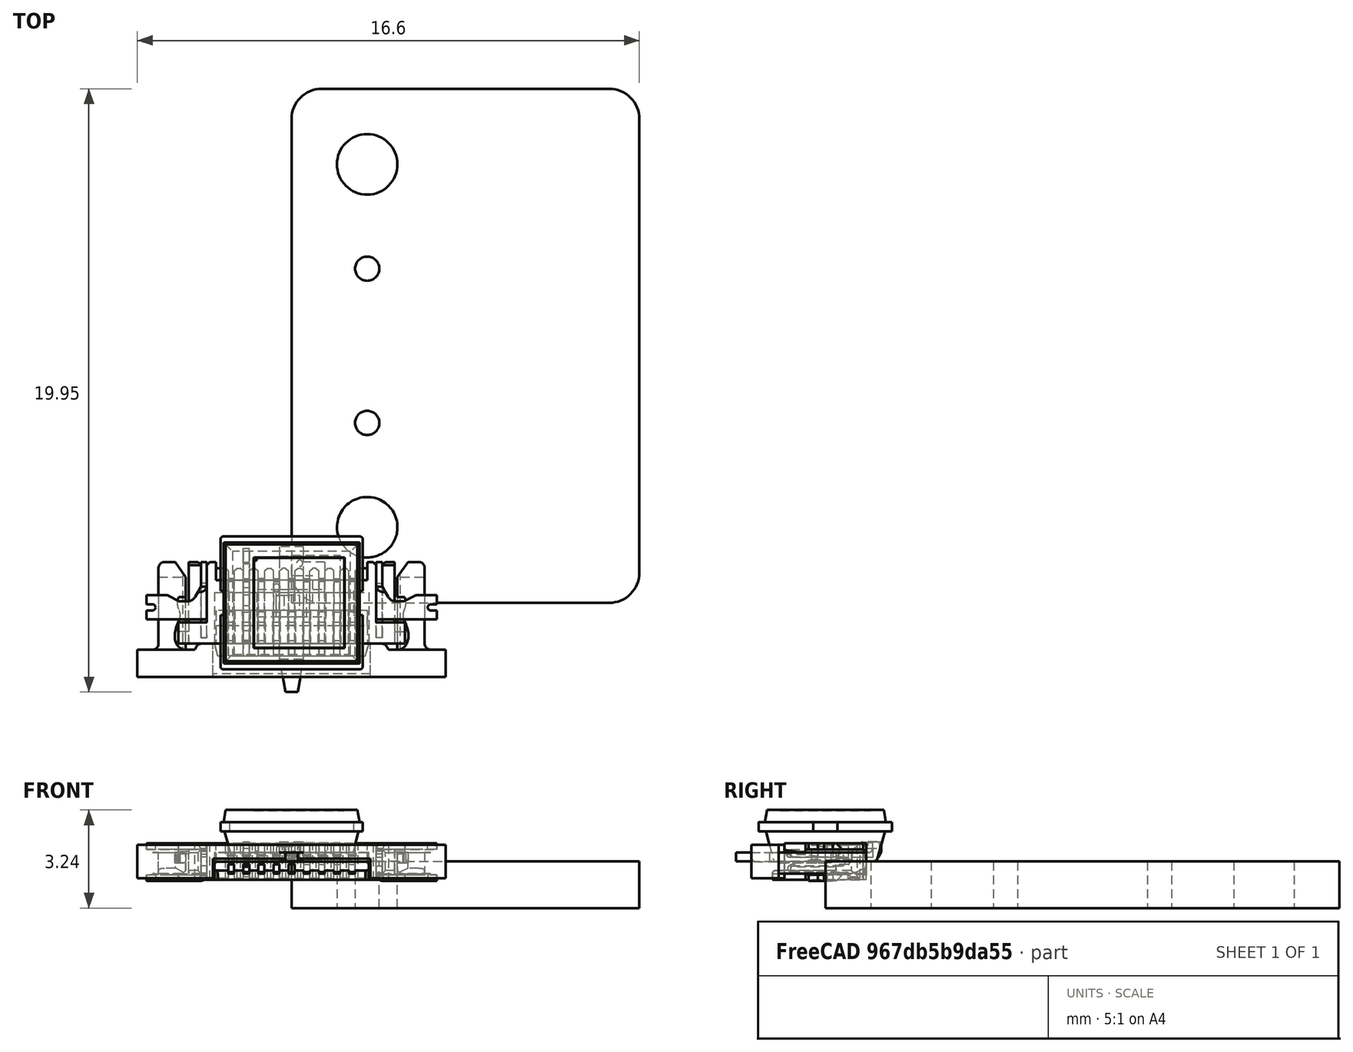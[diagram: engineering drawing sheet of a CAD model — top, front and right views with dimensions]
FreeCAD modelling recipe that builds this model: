
FCSTD DOCUMENT  (FreeCAD 0.20R29603 (Git))
Label: sensor-PCB
License: All rights reserved
LicenseURL: http://en.wikipedia.org/wiki/All_rights_reserved
objects: Part::Feature×21, App::Part×16, App::Link×15, Part::Compound2×3, PartDesign::SubShapeBinder×2, PartDesign::CoordinateSystem×2, App::FeaturePython×1, PartDesign::Body×1
note: 26 computed .brp shape members not serialized (recipe doc carries the construction recipe); baked Part::Feature solids carry a one-line shape summary decoded from their .brp

FEATURE [App::FeaturePython] Constraints  # WARN: FeaturePython — macro-defined, semantics opaque (R4)
  _Version = 1
FEATURE [App::Link] Link  label="ball001"
  LinkPlacement = pos=(0,0.5,0.125) rot=(0,0,1;0rad)
  LinkedObject = -> Solid002
  Placement = pos=(0,0.5,0.125) rot=(0,0,1;0rad)
FEATURE [App::Link] Link001  label="ball002"
  LinkPlacement = pos=(0.5,0.5,0.125) rot=(0,0,1;0rad)
  LinkedObject = -> Solid002
  Placement = pos=(0.5,0.5,0.125) rot=(0,0,1;0rad)
FEATURE [App::Link] Link002  label="ball003"
  LinkPlacement = pos=(-0.5,0,0.125) rot=(0,0,1;0rad)
  LinkedObject = -> Solid002
  Placement = pos=(-0.5,0,0.125) rot=(0,0,1;0rad)
FEATURE [App::Link] Link003  label="ball004"
  LinkPlacement = pos=(0,0,0.125) rot=(0,0,1;0rad)
  LinkedObject = -> Solid002
  Placement = pos=(0,0,0.125) rot=(0,0,1;0rad)
FEATURE [App::Link] Link004  label="ball005"
  LinkPlacement = pos=(0.5,0,0.125) rot=(0,0,1;0rad)
  LinkedObject = -> Solid002
  Placement = pos=(0.5,0,0.125) rot=(0,0,1;0rad)
FEATURE [App::Link] Link005  label="ball006"
  LinkPlacement = pos=(-0.5,-0.5,0.125) rot=(0,0,1;0rad)
  LinkedObject = -> Solid002
  Placement = pos=(-0.5,-0.5,0.125) rot=(0,0,1;0rad)
FEATURE [App::Link] Link006  label="ball007"
  LinkPlacement = pos=(0,-0.5,0.125) rot=(0,0,1;0rad)
  LinkedObject = -> Solid002
  Placement = pos=(0,-0.5,0.125) rot=(0,0,1;0rad)
FEATURE [App::Link] Link007  label="ball008"
  LinkPlacement = pos=(0.5,-0.5,0.125) rot=(0,0,1;0rad)
  LinkedObject = -> Solid002
  Placement = pos=(0.5,-0.5,0.125) rot=(0,0,1;0rad)
FEATURE [App::Link] Link008  label="Terminal001"
  LinkPlacement = pos=(1.2,0.45,0) rot=(0,0,1;3.14159rad)
  LinkedObject = -> Part004
  Placement = pos=(1.2,0.45,0) rot=(0,0,1;3.14159rad)
FEATURE [App::Link] Link009  label="68X1XX183X22_Pin_TOP001"
  LinkPlacement = pos=(-0.4,1.05,-0.045) rot=(0,0,1;1.5708rad)
  LinkedObject = -> Solid010
  Placement = pos=(-0.4,1.05,-0.045) rot=(0,0,1;1.5708rad)
FEATURE [App::Link] Link010  label="68X1XX183X22_Pin_TOP002"
  LinkPlacement = pos=(0.6,1.05,-0.045) rot=(0,0,1;1.5708rad)
  LinkedObject = -> Solid010
  Placement = pos=(0.6,1.05,-0.045) rot=(0,0,1;1.5708rad)
FEATURE [App::Link] Link011  label="68X1XX183X22_Pin_TOP003"
  LinkPlacement = pos=(1.6,1.05,-0.045) rot=(0,0,1;1.5708rad)
  LinkedObject = -> Solid010
  Placement = pos=(1.6,1.05,-0.045) rot=(0,0,1;1.5708rad)
FEATURE [App::Link] Link012  label="pin001"
  LinkPlacement = pos=(0.375,3e-16,-3e-16) rot=(0,0,1;3.14159rad)
  LinkedObject = -> Solid019
  Placement = pos=(0.375,3e-16,-3e-16) rot=(0,0,1;3.14159rad)
FEATURE [App::Link] Link013  label="1x0.5x0.5x0.026"
  LinkPlacement = pos=(4.25098,5.93,0) rot=(0,0,-1;1.5708rad)
  LinkedObject = -> Part011
  Placement = pos=(4.25098,5.93,0) rot=(0,0,-1;1.5708rad)
FEATURE [App::Link] Link014  label="1x0.5x0.5x0.027"
  LinkPlacement = pos=(4.88605,11.5101,0) rot=(0,0,1;0rad)
  LinkedObject = -> Part011
  Placement = pos=(4.88605,11.5101,0) rot=(0,0,1;0rad)
FEATURE [App::Part] Part013  label="C2"
  Group = -> [Link013]
  Origin = -> Origin013
FEATURE [App::Part] Part015  label="C1"
  Group = -> [Link014]
  Origin = -> Origin015
FEATURE [Part::Feature] Shell  label="Open_CASCADE_STEP_translator_6.8_1.1"
  Placement = pos=(-0.81,-0.79,0) rot=(0,0,1;0rad)
  shape: bbox 0.2025 x 0.2025 x 2e-07 mm, 1 faces, 0 solids (baked)
FEATURE [Part::Feature] Solid  label="Open CASCADE STEP translator 6.8 2.1.1"
  Placement = pos=(0,0,-1.54144) rot=(0,0,1;0rad)
  shape: bbox 11.5 x 17 x 1.541 mm, 14 faces (baked)
FEATURE [App::Part] Part  label="Board"
  Group = -> [Solid]
  Origin = -> Origin
FEATURE [Part::Feature] Solid001  label="Open_CASCADE_STEP_translator_6.8_1.2.1"
  shape: bbox 1.62 x 1.58 x 0.475 mm, 8 faces (baked)
FEATURE [App::Part] Part001  label="Body"
  Group = -> [Solid001]
  Origin = -> Origin001
  Placement = pos=(-0.81,-0.79,0) rot=(0,0,1;0rad)
FEATURE [Part::Feature] Solid002  label="ball"
  Placement = pos=(-0.5,0.5,0.125) rot=(0,0,1;0rad)
  shape: bbox 0.25 x 0.25 x 0.25 mm, 1 faces (baked)
FEATURE [App::Part] Part002  label="5833252656"
  Group = -> [Shell,Part001,Solid002,Link,Link001,Link002,Link003,Link004,Link005,Link006,Link007]
  Origin = -> Origin002
  Placement = pos=(4.878,8.47,0) rot=(0,0,1;1.5708rad)
FEATURE [App::Part] Part003  label="U1"
  Group = -> [Part002]
  Origin = -> Origin003
FEATURE [Part::Feature] Solid003  label="Mid_Body"
  Placement = pos=(-1.2,-0.45,0) rot=(0,0,1;0rad)
  shape: bbox 2.28 x 0.9 x 0.48 mm, 6 faces (baked)
FEATURE [Part::Feature] Solid004  label="Open_CASCADE_STEP_translator_6.8_3.2.1"
  shape: bbox 0.7 x 0.9 x 0.6 mm, 10 faces (baked)
FEATURE [App::Part] Part004  label="Terminal"
  Group = -> [Solid004]
  Origin = -> Origin004
  Placement = pos=(-1.2,-0.45,0) rot=(0,0,1;0rad)
FEATURE [Part::Feature] Solid005  label="Mark"
  Placement = pos=(-0.5,-0.45,0.54) rot=(0,0,1;0rad)
  shape: bbox 1 x 0.9 x 0.06 mm, 6 faces (baked)
FEATURE [App::Part] Part005  label="5983538608"
  Group = -> [Solid003,Part004,Link008,Solid005]
  Origin = -> Origin005
  Placement = pos=(5.6,5.5,0) rot=(0,0,1;1.5708rad)
FEATURE [App::Part] Part006  label="R1"
  Group = -> [Part005]
  Origin = -> Origin006
FEATURE [Part::Feature] Solid006  label="68x109183x22"
  shape: bbox 7.5 x 3.1 x 1.2 mm, 237 faces (baked)
FEATURE [Part::Feature] Solid007  label="68x109183x22_Actuator"
  Placement = pos=(-1.67e-13,-2,5e-15) rot=(1,0,0;3.14159rad)
  shape: bbox 10.2 x 3.8 x 1.1 mm, 117 faces (baked)
FEATURE [Part::Feature] Solid008  label="68X1xx183x22_Solder_Pad2"
  Placement = pos=(2.8,-0.25,-0.02) rot=(0,0,-1;1.5708rad)
  shape: bbox 2 x 2.5 x 1.24 mm, 61 faces (baked)
FEATURE [Part::Feature] Solid009  label="68X1XX183X22_Solder_Pad"
  Placement = pos=(-2.8,-0.25,-0.02) rot=(0.707107,-0.707107,0;3.14159rad)
  shape: bbox 2 x 2.5 x 1.24 mm, 61 faces (baked)
FEATURE [Part::Feature] Solid010  label="68X1XX183X22_Pin_TOP"
  Placement = pos=(-1.4,1.05,-0.045) rot=(0,0,1;1.5708rad)
  shape: bbox 0.2 x 3.097 x 1.15 mm, 38 faces (baked)
FEATURE [App::Part] Part007  label="686104183422"
  Group = -> [Solid006,Solid007,Solid008,Solid009,Solid010,Link009,Link010,Link011]
  Origin = -> Origin007
  Placement = pos=(8.95005,8.49992,0.640001) rot=(0.707107,-0.707107,0;3.14159rad)
FEATURE [App::Part] Part008  label="J1"
  Group = -> [Part007]
  Origin = -> Origin008
FEATURE [Part::Feature] Solid011
  shape: bbox 4.436 x 3.936 x 1 mm, 6 faces (baked)
FEATURE [Part::Feature] Solid012
  shape: bbox 4.7 x 4.4 x 0.3 mm, 18 faces (baked)
FEATURE [Part::Feature] Solid013
  shape: bbox 4.5 x 4 x 0.4 mm, 21 faces (baked)
FEATURE [Part::Compound2] Compound  label="body"
  Links = -> [Solid011,Solid012,Solid013]
  Placement = pos=(-0.585529,0.102898,-0.610932) rot=(0,0,1;0rad)
FEATURE [Part::Feature] Solid014
  shape: bbox 0.8 x 1.1 x 0.3 mm, 6 faces (baked)
FEATURE [Part::Feature] Solid015
  shape: bbox 0.8 x 3.7 x 0.65 mm, 10 faces (baked)
FEATURE [Part::Compound2] Compound001  label="footA"
  Links = -> [Solid014,Solid015]
  Placement = pos=(-3.28553,0.102898,-1.16041) rot=(0.57735,0.57735,0.57735;2.0944rad)
FEATURE [Part::Feature] Solid016
  shape: bbox 0.8 x 1.1 x 0.3 mm, 6 faces (baked)
FEATURE [Part::Feature] Solid017
  shape: bbox 1.5 x 3.7 x 0.65 mm, 14 faces (baked)
FEATURE [Part::Compound2] Compound002  label="footB"
  Links = -> [Solid016,Solid017]
  Placement = pos=(2.11447,0.102898,-1.16093) rot=(0.57735,-0.57735,-0.57735;2.0944rad)
FEATURE [App::Part] Part009  label="BPW34"
  Group = -> [Compound,Compound001,Compound002,Solid012,Solid013,Solid011,Solid014,Solid015,Solid017,Solid016]
  Origin = -> Origin009
  Placement = pos=(2.39719,9.08559,-2.14144) rot=(0.707107,0.707107,0;3.14159rad)
FEATURE [App::Part] Part010  label="D1"
  Group = -> [Part009]
  Origin = -> Origin010
FEATURE [Part::Feature] Solid018  label="base"
  shape: bbox 0.5 x 0.5 x 0.5 mm, 10 faces (baked)
FEATURE [Part::Feature] Solid019  label="pin"
  Placement = pos=(-0.375,0,0) rot=(0,0,1;0rad)
  shape: bbox 0.25 x 0.5 x 0.5 mm, 18 faces (baked)
FEATURE [App::Part] Part011  label="1x0.5x0.5x0.25"
  Group = -> [Solid018,Solid019,Link012]
  Origin = -> Origin011
  Placement = pos=(4.88605,10.3671,0) rot=(0,0,1;0rad)
FEATURE [App::Part] Part012  label="C3"
  Group = -> [Part011]
  Origin = -> Origin012
FEATURE [PartDesign::SubShapeBinder] Binder001
  BindCopyOnChange = 0
  BindMode = 0
  ClaimChildren = false
  Context = -> Part014 [Sensor_shape.Binder001.]
  Fuse = false
  MakeFace = true
  OffsetFill = false
  OffsetIntersection = false
  OffsetJoinType = 0
  OffsetOpenResult = false
  PartialLoad = false
  Relative = true
  Support = -> [Part[Solid.Edge11,Solid.Edge10,Solid.Edge5,Solid.Edge3,Solid.Edge23,Solid.Edge22,Solid.Edge17,Solid.Edge16]]
  _Version = 2
FEATURE [PartDesign::SubShapeBinder] Binder
  BindCopyOnChange = 0
  BindMode = 0
  ClaimChildren = false
  Context = -> Part014 [Sensor_shape.Binder.]
  Fuse = false
  MakeFace = true
  OffsetFill = false
  OffsetIntersection = false
  OffsetJoinType = 0
  OffsetOpenResult = false
  PartialLoad = false
  Relative = true
  Support = -> [Part010[Part009.Compound.Edge96,Part009.Compound.Edge94,Part009.Compound.Edge92,Part009.Compound.Edge90]]
  _Version = 2
FEATURE [PartDesign::CoordinateSystem] Local_CS  label="LCS-Base"
  AttacherType = Attacher::AttachEngine3D
  AttachmentOffset = pos=(0,0,-4) rot=(1,0,0;3.14159rad)
  MapMode = 45
  Placement = pos=(5.75,8.5,-4) rot=(1,0,0;3.14159rad)
  Support = -> [Binder001]
FEATURE [PartDesign::CoordinateSystem] Local_CS001  label="LCS-Diode"
  AttacherType = Attacher::AttachEngine3D
  AttachmentOffset = pos=(0,0,0) rot=(1,0,0;3.14159rad)
  MapMode = 45
  Placement = pos=(2.50009,8.75006,-3.21051) rot=(1,0,0;3.14159rad)
  Support = -> [Binder]
FEATURE [PartDesign::Body] Sensor_shape  label="Sensor-shape"
  Group = -> [Binder001,Binder,Local_CS,Local_CS001]
  Origin = -> Origin016
FEATURE [App::Part] Part014  label="sensor"
  Group = -> [Part,Part003,Part006,Part008,Part010,Part012,Part013,Part015,Sensor_shape]
  Origin = -> Origin014
  Placement = pos=(-2.5,8.75,-3.2) rot=(1,0,0;3.14159rad)
